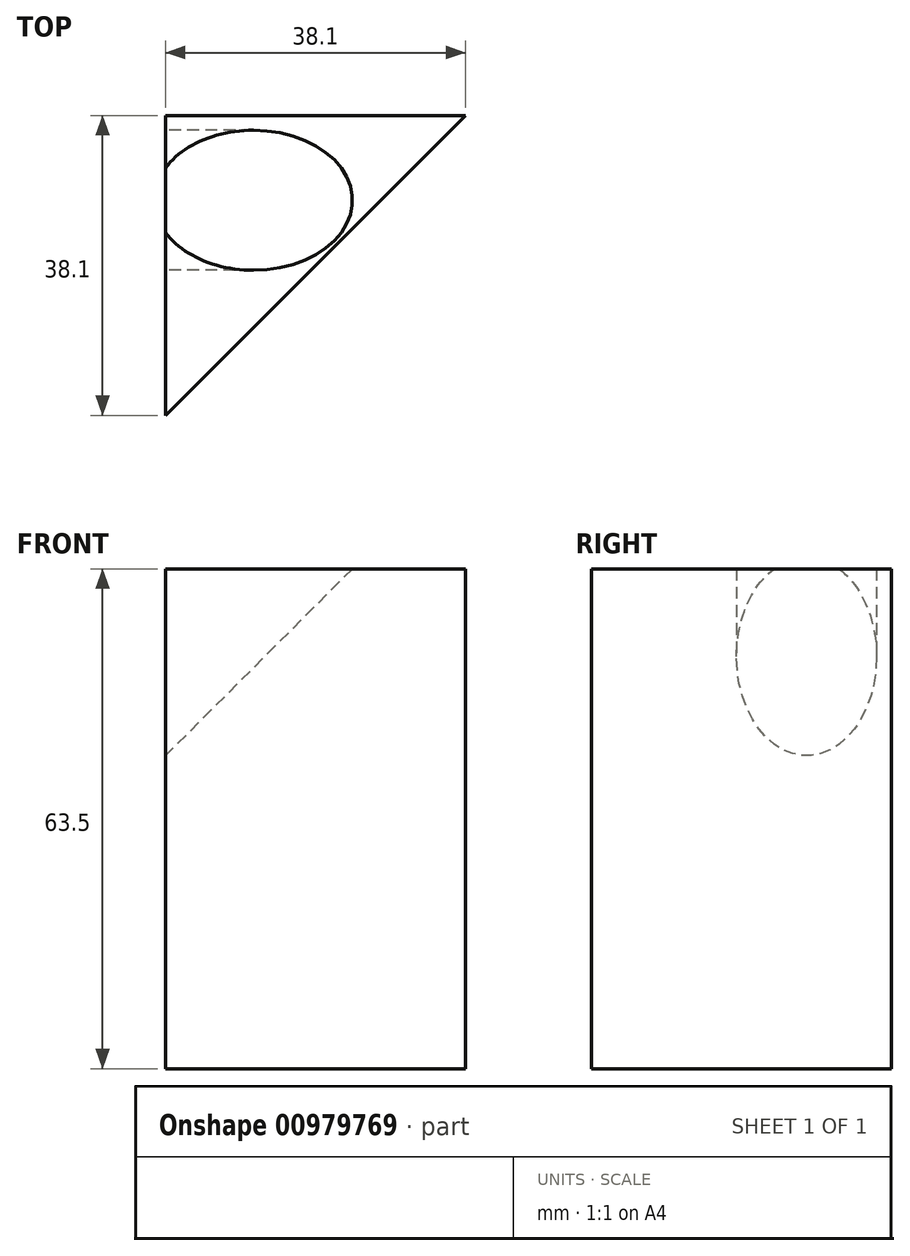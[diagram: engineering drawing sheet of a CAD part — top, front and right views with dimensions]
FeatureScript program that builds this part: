
annotation { "Feature Type Name" : "Feature", "Feature Type Description" : "" }
export const myFeature = defineFeature(function(context is Context, id is Id, definition is map)
    precondition{}
    {
        {
            var Q0;
            Q0=qCreatedBy(makeId("Front.planeOp"),FACE);
            var sketch = newSketch(context, id + "F0", { "sketchPlane" : qUnion([Q0])});
            skLineSegment(sketch, "E0", {"start": v(0, 0) * mm, "end": v(0, -63.5) * mm});
            skLineSegment(sketch, "E1", {"start": v(0, -63.5) * mm, "end": v(-38.1, -63.5) * mm});
            skLineSegment(sketch, "E2", {"start": v(-38.1, -63.5) * mm, "end": v(-38.1, 0) * mm});
            skLineSegment(sketch, "E3", {"start": v(-38.1, 0) * mm, "end": v(0, 0) * mm});
            skSolve(sketch);
        }
        {
            var Q0;
            Q0 = qSketchRegion(id + "F0", true);
            extrude(context, id + "F1", {"entities" : qUnion([Q0]), "depth" : 38.1 * mm, "offsetDistance" : 25.4 * mm});
        }
        {
            var Q0;
            Q0=makeQuery(id+"F1.opExtrude","SWEPT_FACE",FACE,{"disambiguationData":[OSD([sQuery(id+"F0.wireOp",EDGE,"E0")])]});
            var sketch = newSketch(context, id + "F2", { "sketchPlane" : qUnion([Q0])});
            skCircle(sketch, "E4", {"center": v(-31.75, -6.35) * mm, "radius": 3.18 * mm});
            skCircle(sketch, "E5", {"center": v(-6.35, -6.35) * mm, "radius": 3.18 * mm});
            skCircle(sketch, "E6", {"center": v(-31.75, -57.15) * mm, "radius": 3.18 * mm});
            skCircle(sketch, "E7", {"center": v(-6.35, -57.15) * mm, "radius": 3.18 * mm});
            skCircle(sketch, "E8", {"center": v(-19.05, -15.24) * mm, "radius": 8.9 * mm});
            skPoint(sketch, "E9", {"position": v(-19.05, 0) * mm});
            skLineSegment(sketch, "E10", {"start": v(-3.32, -15.24) * mm, "end": v(-63.22, -15.24) * mm, "construction": true});
            skSolve(sketch);
        }
        {
            var Q0;
            Q0=sQuery(id+"F2.wireOp",EDGE,"E10");
            cPlane(context, id + "F3", {"entities" : qUnion([Q0]), "cplaneType" : CPlaneType.LINE_ANGLE, "offset" : 25.4 * mm, "angle" : 45 * degree, "oppositeDirection" : true, "width" : 152.4 * mm, "height" : 152.4 * mm});
        }
        {
            var Q0;
            Q0=qCreatedBy(id+"F3.planeOp",FACE);
            var sketch = newSketch(context, id + "F4", { "sketchPlane" : qUnion([Q0])});
            skCircle(sketch, "E11", {"center": v(10.78, 19.05) * mm, "radius": 8.9 * mm});
            skSolve(sketch);
        }
        {
            var Q0;
            Q0=makeQuery(id+"F4.imprint","IMPRINT",FACE,{"disambiguationData":[TD([[makeQuery(id+"F4.imprint","IMPRINT",EDGE,{"derivedFrom":sQuery(id+"F4.wireOp",EDGE,"E11")}),1.0]])]});
            extrude(context, id + "F5", {"entities" : qUnion([Q0]), "operationType" : NewBodyOperationType.REMOVE, "oppositeDirection" : true, "depth" : 50.8 * mm, "offsetDistance" : 25.4 * mm, "hasSecondDirection" : true, "secondDirectionOppositeDirection" : false, "secondDirectionDepth" : 76.2 * mm});
        }
        {
            var Q0;
            Q0=makeQuery(id+"F1.opExtrude","SWEPT_FACE",FACE,{"disambiguationData":[OSD([sQuery(id+"F0.wireOp",EDGE,"E3")])]});
            var sketch = newSketch(context, id + "F6", { "sketchPlane" : qUnion([Q0])});
            skLineSegment(sketch, "E12", {"start": v(0, 0) * mm, "end": v(-38.1, -38.1) * mm});
            skLineSegment(sketch, "E13", {"start": v(-38.1, -38.1) * mm, "end": v(0, -38.1) * mm});
            skLineSegment(sketch, "E14", {"start": v(0, -38.1) * mm, "end": v(0, 0) * mm});
            skSolve(sketch);
        }
        {
            var Q0;
            Q0=makeQuery(id+"F6.imprint","IMPRINT",FACE,{"disambiguationData":[TD([[makeQuery(id+"F6.imprint","IMPRINT",EDGE,{"derivedFrom":sQuery(id+"F6.wireOp",EDGE,"E12")}),1.0]])]});
            extrude(context, id + "F7", {"entities" : qUnion([Q0]), "operationType" : NewBodyOperationType.REMOVE, "oppositeDirection" : true, "depth" : 76.2 * mm, "offsetDistance" : 25.4 * mm});
        }
    });
